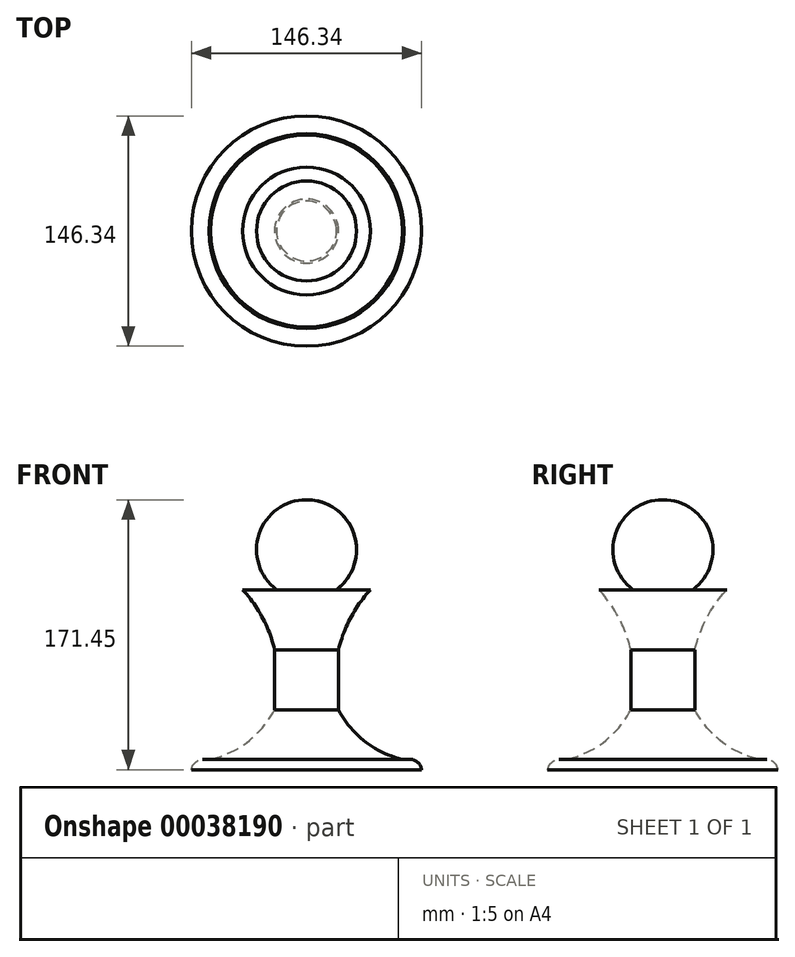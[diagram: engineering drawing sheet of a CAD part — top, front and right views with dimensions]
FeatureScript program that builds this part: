
annotation { "Feature Type Name" : "Feature", "Feature Type Description" : "" }
export const myFeature = defineFeature(function(context is Context, id is Id, definition is map)
    precondition{}
    {
        {
            var Q0;
            Q0=qCreatedBy(makeId("Front.planeOp"),FACE);
            var sketch = newSketch(context, id + "F0", { "sketchPlane" : qUnion([Q0])});
            skLineSegment(sketch, "E0", {"start": v(20.32, 16.6) * mm, "end": v(20.32, -21.5) * mm});
            skLineSegment(sketch, "E1", {"start": v(0, -59.6) * mm, "end": v(73.17, -59.6) * mm});
            skArc(sketch, "E2", {"start": v(40.64, 54.7) * mm, "mid": v(27.99, 36.98) * mm, "end": v(20.32, 16.6) * mm});
            skPoint(sketch, "E2.third.point", {"position": v(185.86, 0) * mm});
            skPoint(sketch, "E3.third.point", {"position": v(145.2, -35.14) * mm});
            skPoint(sketch, "E4.MirrorCS.end.orphan", {"position": v(60.96, 162.45) * mm});
            skPoint(sketch, "E4.MirrorCS.start.orphan", {"position": v(20.32, 130.9) * mm});
            skPoint(sketch, "E5.MirrorCS.end.orphan", {"position": v(20.32, 92.8) * mm});
            skPoint(sketch, "E5.MirrorCS.start.orphan", {"position": v(40.64, 54.7) * mm});
            skPoint(sketch, "E6.center.orphan", {"position": v(0, 54.7) * mm});
            skArc(sketch, "E7", {"start": v(19.05, 54.7) * mm, "mid": v(30.12, 90.14) * mm, "end": v(0, 111.85) * mm});
            skLineSegment(sketch, "E8", {"start": v(40.64, 54.7) * mm, "end": v(19.05, 54.7) * mm});
            skFitSpline(sketch, "E9", {"points": [v(60.96, -53.06) * mm, v(64.02, -53.06) * mm, v(67.12, -53.06) * mm, v(70.02, -54.53) * mm, v(71.95, -56.47) * mm, v(73.17, -59.6) * mm], "startDerivative": vector(15.35, -0.47) * mm, "endDerivative": vector(4.82, -16.31) * mm});
            skPoint(sketch, "E10.start.orphan", {"position": v(0, -46.8) * mm});
            skPoint(sketch, "E11.end.orphan", {"position": v(0, -53.06) * mm});
            skArc(sketch, "E12", {"start": v(61.96, -53.08) * mm, "mid": v(61.97, -53.09) * mm, "end": v(61.98, -53.09) * mm});
            skPoint(sketch, "E12.third.point", {"position": v(135.7, 25) * mm});
            skArc(sketch, "E13", {"start": v(20.32, -21.5) * mm, "mid": v(37.17, -41.76) * mm, "end": v(60.96, -53.06) * mm});
            skPoint(sketch, "E13.third.point", {"position": v(15.1, -7.4) * mm});
            skLineSegment(sketch, "E14", {"start": v(60.96, -53.06) * mm, "end": v(61.98, -53.09) * mm});
            skLineSegment(sketch, "E15", {"start": v(0, 111.85) * mm, "end": v(0, -59.6) * mm});
            skSolve(sketch);
        }
        {
            var Q0;
            Q0=makeQuery(id+"F0.imprint","IMPRINT",FACE,{"disambiguationData":[TD([[makeQuery(id+"F0.imprint","IMPRINT",EDGE,{"derivedFrom":sQuery(id+"F0.wireOp",EDGE,"E0")}),-1.0]])]});
            var Q1;
            Q1=sQuery(id+"F0.wireOp",EDGE,"E15");
            revolve(context, id + "F1", {"entities" : qUnion([Q0]), "axis" : qUnion([Q1]), "revolveType" : RevolveType.FULL});
        }
    });
